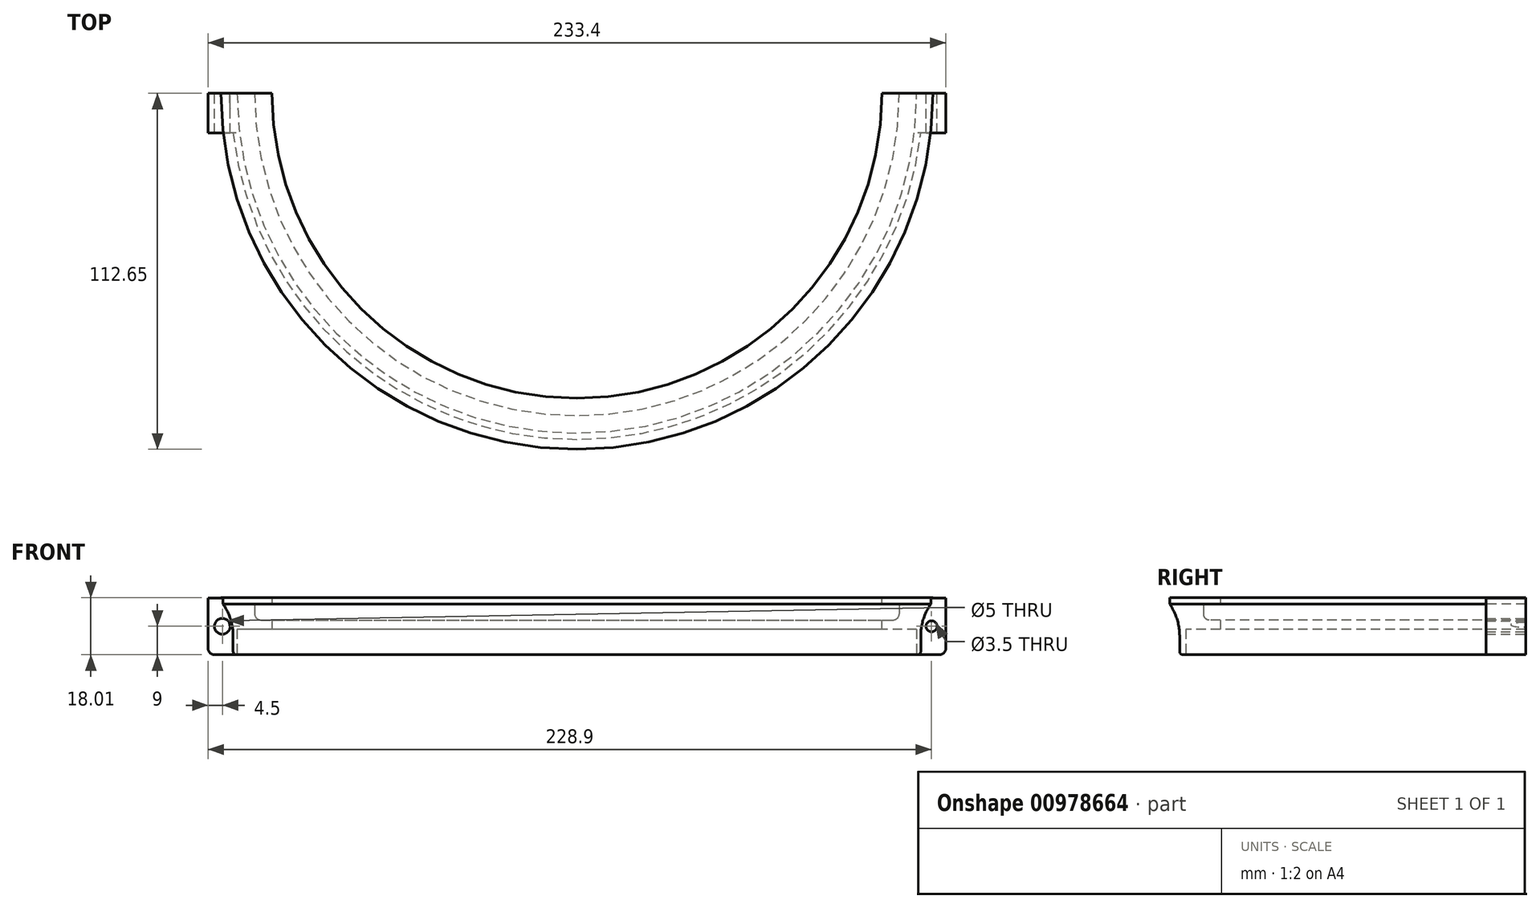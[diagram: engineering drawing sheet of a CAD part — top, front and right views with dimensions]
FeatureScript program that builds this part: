
annotation { "Feature Type Name" : "Feature", "Feature Type Description" : "" }
export const myFeature = defineFeature(function(context is Context, id is Id, definition is map)
    precondition{}
    {
        {
            var Q0;
            Q0=qCreatedBy(makeId("Front.planeOp"),FACE);
            var sketch = newSketch(context, id + "F0", { "sketchPlane" : qUnion([Q0])});
            skLineSegment(sketch, "E0", {"start": v(0, 0) * mm, "end": v(-105.5, 0) * mm});
            skLineSegment(sketch, "E1", {"start": v(-96.5, -3) * mm, "end": v(-107.5, -3) * mm});
            skLineSegment(sketch, "E2", {"start": v(-107.5, -3) * mm, "end": v(-107.5, -11) * mm});
            skLineSegment(sketch, "E3", {"start": v(-107.5, -11) * mm, "end": v(-109.5, -11) * mm});
            skLineSegment(sketch, "E4", {"start": v(-109.5, -11) * mm, "end": v(-109.5, -5) * mm});
            skLineSegment(sketch, "E5", {"start": v(-112.65, 7) * mm, "end": v(-112.65, 5) * mm});
            skLineSegment(sketch, "E6", {"start": v(0, -15.27) * mm, "end": v(0, 14.73) * mm});
            skArc(sketch, "E7", {"start": v(-109.5, -5) * mm, "mid": v(-110.3, 0.25) * mm, "end": v(-112.65, 5) * mm});
            skLineSegment(sketch, "E8", {"start": v(-96.5, -3) * mm, "end": v(-96.5, 7) * mm});
            skLineSegment(sketch, "E9", {"start": v(-112.65, 7) * mm, "end": v(-96.5, 7) * mm});
            skSolve(sketch);
        }
        {
            var Q0;
            Q0=qSketchRegion(id+"F0",true);
            var Q1;
            Q1=sQuery(id+"F0.wireOp",EDGE,"E6");
            revolve(context, id + "F1", {"surfaceOperationType" : NewSurfaceOperationType.NEW, "entities" : qUnion([Q0]), "axis" : qUnion([Q1]), "revolveType" : RevolveType.FULL});
        }
        {
            var Q0;
            Q0=qCreatedBy(makeId("Top.planeOp"),FACE);
            var sketch = newSketch(context, id + "F2", { "sketchPlane" : qUnion([Q0])});
            skCircle(sketch, "E10", {"center": v(0, 0) * mm, "radius": 102 * mm});
            skSolve(sketch);
        }
        {
            var Q0;
            Q0=qSketchRegion(id+"F2",true);
            extrude(context, id + "F3", {"entities" : qUnion([Q0]), "operationType" : NewBodyOperationType.REMOVE, "depth" : 5 * mm, "offsetDistance" : 25 * mm});
        }
        {
            var Q0;
            Q0=makeQuery(id+"F1.opRevolve","SWEPT_EDGE",EDGE,{"disambiguationData":[OSD([sQuery(id+"F0.wireOp",EDGE,"E3"),sQuery(id+"F0.wireOp",EDGE,"E4")])]});
            fillet(context, id + "F4", {"entities" : qUnion([Q0]), "radius" : 1 * mm, "tangentPropagation" : true, "allowEdgeOverflow" : false});
        }
        {
            var Q0;
            Q0=qCreatedBy(makeId("Front.planeOp"),FACE);
            var sketch = newSketch(context, id + "F5", { "sketchPlane" : qUnion([Q0])});
            skLineSegment(sketch, "E11.bottom", {"start": v(-107.7, 7) * mm, "end": v(-116.7, 7) * mm});
            skLineSegment(sketch, "E11.top", {"start": v(-107.7, -11) * mm, "end": v(-116.7, -11) * mm});
            skLineSegment(sketch, "E11.left", {"start": v(-107.7, 7) * mm, "end": v(-107.7, -11) * mm});
            skLineSegment(sketch, "E11.right", {"start": v(-116.7, 7) * mm, "end": v(-116.7, -11) * mm});
            skCircle(sketch, "E12", {"center": v(-112.2, -2) * mm, "radius": 2.5 * mm});
            skSolve(sketch);
        }
        {
            var Q0;
            Q0=qCreatedBy(makeId("Front.planeOp"),FACE);
            var sketch = newSketch(context, id + "F6", { "sketchPlane" : qUnion([Q0])});
            skLineSegment(sketch, "E13.bottom", {"start": v(116.7, 7) * mm, "end": v(107.7, 7) * mm});
            skLineSegment(sketch, "E13.top", {"start": v(116.7, -11) * mm, "end": v(107.7, -11) * mm});
            skLineSegment(sketch, "E13.left", {"start": v(116.7, 7) * mm, "end": v(116.7, -11) * mm});
            skLineSegment(sketch, "E13.right", {"start": v(107.7, 7) * mm, "end": v(107.7, -11) * mm});
            skCircle(sketch, "E14", {"center": v(112.2, -2) * mm, "radius": 1.75 * mm});
            skSolve(sketch);
        }
        {
            var Q0;
            Q0=qSketchRegion(id+"F5",true);
            extrude(context, id + "F7", {"entities" : qUnion([Q0]), "operationType" : NewBodyOperationType.ADD, "endBound" : BoundingType.SYMMETRIC, "depth" : 25 * mm, "offsetDistance" : 25 * mm});
        }
        {
            var Q0;
            Q0=qSketchRegion(id+"F6",true);
            extrude(context, id + "F8", {"entities" : qUnion([Q0]), "operationType" : NewBodyOperationType.ADD, "endBound" : BoundingType.SYMMETRIC, "depth" : 25 * mm, "offsetDistance" : 25 * mm});
        }
        {
            var Q0;
            Q0=qCreatedBy(makeId("Front.planeOp"),FACE);
            var sketch = newSketch(context, id + "F9", { "sketchPlane" : qUnion([Q0])});
            skLineSegment(sketch, "E15.bottom", {"start": v(-124.88, 17.7) * mm, "end": v(125.12, 17.7) * mm});
            skLineSegment(sketch, "E15.top", {"start": v(-124.88, -82.3) * mm, "end": v(125.12, -82.3) * mm});
            skLineSegment(sketch, "E15.left", {"start": v(-124.88, 17.7) * mm, "end": v(-124.88, -82.3) * mm});
            skLineSegment(sketch, "E15.right", {"start": v(125.12, 17.7) * mm, "end": v(125.12, -82.3) * mm});
            skSolve(sketch);
        }
        {
            var Q0;
            Q0=qSketchRegion(id+"F9",true);
            extrude(context, id + "F10", {"entities" : qUnion([Q0]), "operationType" : NewBodyOperationType.REMOVE, "oppositeDirection" : true, "depth" : 150 * mm, "offsetDistance" : 25 * mm});
        }
        {
            var Q0;
            Q0=makeQuery(id+"F3.boolean.opBoolean","COPY",EDGE,{"derivedFrom":makeQuery(id+"F3.opExtrude","CAP_EDGE",EDGE,{"disambiguationData":[OSD([sQuery(id+"F2.wireOp",EDGE,"E10")])],"isStart":true})});
            fillet(context, id + "F11", {"entities" : qUnion([Q0]), "radius" : 2 * mm, "tangentPropagation" : true, "allowEdgeOverflow" : false});
        }
        {
            var Q0;
            Q0=makeQuery(id+"F8.opExtrude","SWEPT_EDGE",EDGE,{"disambiguationData":[OSD([sQuery(id+"F6.wireOp",EDGE,"E13.top"),sQuery(id+"F6.wireOp",EDGE,"E13.left")])]});
            var Q1;
            Q1=makeQuery(id+"F7.opExtrude","SWEPT_EDGE",EDGE,{"disambiguationData":[OSD([sQuery(id+"F5.wireOp",EDGE,"E11.top"),sQuery(id+"F5.wireOp",EDGE,"E11.right")])]});
            fillet(context, id + "F12", {"entities" : qUnion([Q0, Q1]), "radius" : 2 * mm, "tangentPropagation" : true, "allowEdgeOverflow" : false});
        }
    });
